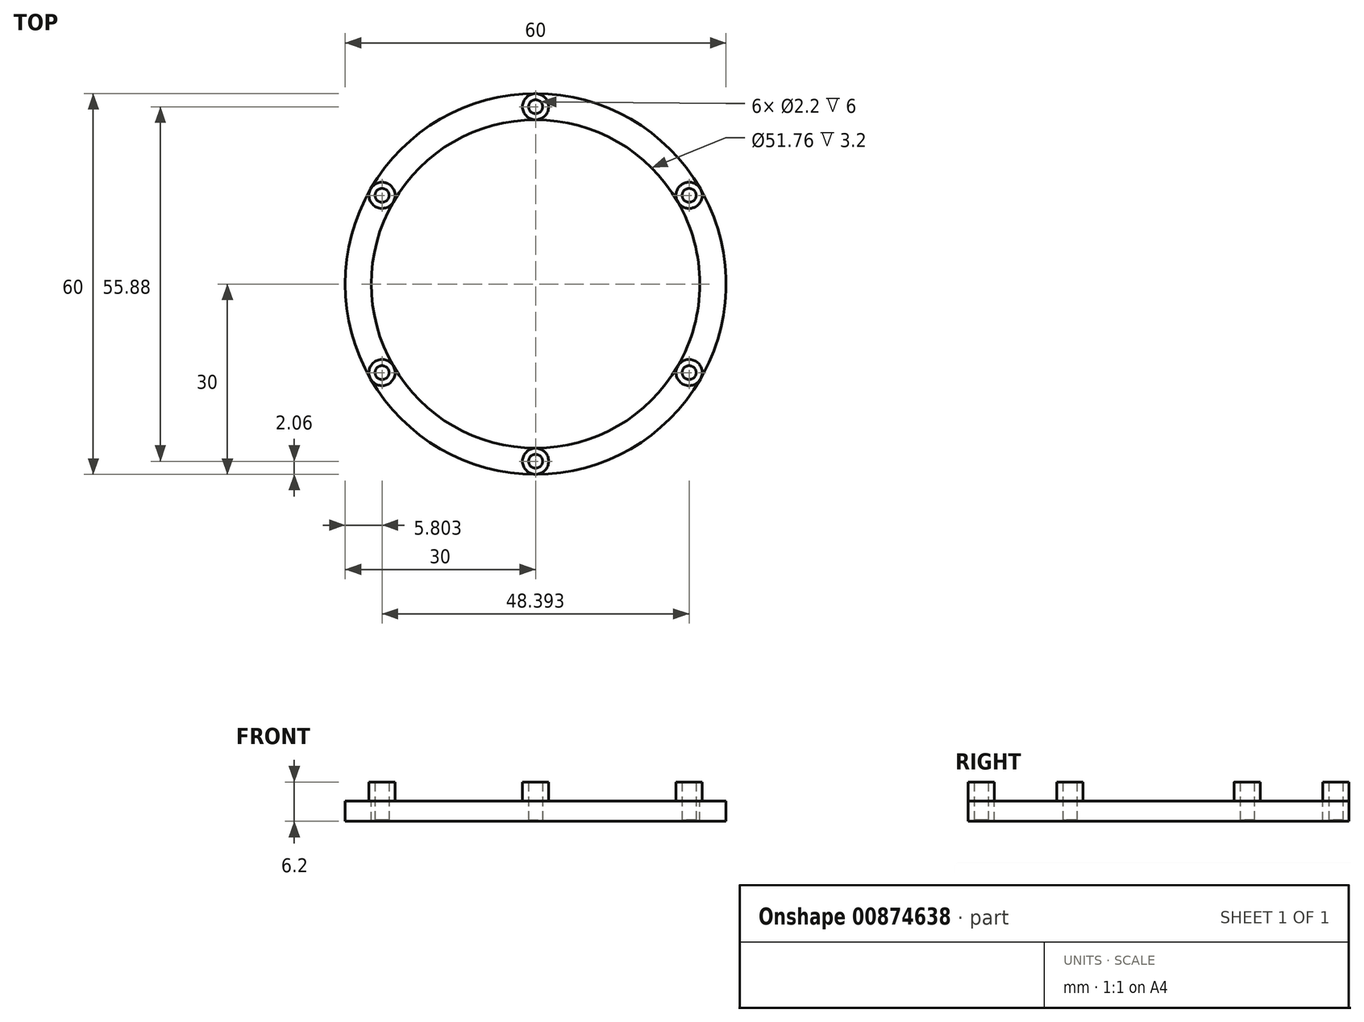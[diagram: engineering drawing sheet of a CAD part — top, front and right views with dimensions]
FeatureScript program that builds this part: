
annotation { "Feature Type Name" : "Feature", "Feature Type Description" : "" }
export const myFeature = defineFeature(function(context is Context, id is Id, definition is map)
    precondition{}
    {
        {
            assignVariable(context, id + "F0", {"name" : "numHoles", "anyValue" : 6});
        }
        {
            var Q0;
            Q0=qCreatedBy(makeId("Top.planeOp"),FACE);
            var sketch = newSketch(context, id + "F1", { "sketchPlane" : qUnion([Q0])});
            skCircle(sketch, "E0", {"center": v(0, 0) * mm, "radius": 30 * mm});
            skCircle(sketch, "E1", {"center": v(0, 0) * mm, "radius": 25.88 * mm});
            skLineSegment(sketch, "E2", {"start": v(0, 21.68) * mm, "end": v(0, -38.1) * mm, "construction": true});
            skCircle(sketch, "E3", {"center": v(0, 27.94) * mm, "radius": 1.1 * mm});
            skCircle(sketch, "E4", {"center": v(0, 27.94) * mm, "radius": 2.06 * mm});
            skLineSegment(sketch, "E5", {"start": v(0, 30) * mm, "end": v(0, 25.88) * mm, "construction": true});
            skSolve(sketch);
        }
        {
            var Q0;
            Q0=qCreatedBy(makeId("Right.planeOp"),FACE);
            var sketch = newSketch(context, id + "F2", { "sketchPlane" : qUnion([Q0])});
            skLineSegment(sketch, "E6", {"start": v(0, 37.6) * mm, "end": v(0, -34.54) * mm, "construction": true});
            skSolve(sketch);
        }
        {
            var Q0;
            {var subQ0=sQuery(id+"F1.wireOp",EDGE,"E0");Q0=makeQuery(id+"F1.imprint","IMPRINT",FACE,{"disambiguationData":[TD([[makeQuery(id+"F1.imprint","IMPRINT",EDGE,{"derivedFrom":subQ0}),1.0]])]});}
            var Q1;
            Q1=makeQuery(id+"F1.imprint","IMPRINT",FACE,{"disambiguationData":[TD([[makeQuery(id+"F1.imprint","IMPRINT",EDGE,{"derivedFrom":sQuery(id+"F1.wireOp",EDGE,"E3")}),-1.0]])]});
            var Q2;
            Q2=makeQuery(id+"F1.imprint","IMPRINT",FACE,{"disambiguationData":[TD([[makeQuery(id+"F1.imprint","IMPRINT",EDGE,{"derivedFrom":sQuery(id+"F1.wireOp",EDGE,"E3")}),1.0]])]});
            extrude(context, id + "F3", {"entities" : qUnion([Q0, Q1, Q2]), "oppositeDirection" : true, "depth" : 0.2 * mm, "offsetDistance" : 25 * mm});
        }
        {
            var Q0;
            {var subQ0=sQuery(id+"F1.wireOp",EDGE,"E0");Q0=makeQuery(id+"F1.imprint","IMPRINT",FACE,{"disambiguationData":[TD([[makeQuery(id+"F1.imprint","IMPRINT",EDGE,{"derivedFrom":subQ0}),1.0]])]});}
            var Q1;
            Q1=makeQuery(id+"F1.imprint","IMPRINT",FACE,{"disambiguationData":[TD([[makeQuery(id+"F1.imprint","IMPRINT",EDGE,{"derivedFrom":sQuery(id+"F1.wireOp",EDGE,"E3")}),-1.0]])]});
            var Q2;
            Q2=makeQuery(id+"F1.imprint","IMPRINT",FACE,{"disambiguationData":[TD([[makeQuery(id+"F1.imprint","IMPRINT",EDGE,{"derivedFrom":sQuery(id+"F1.wireOp",EDGE,"E3")}),1.0]])]});
            extrude(context, id + "F4", {"entities" : qUnion([Q0, Q1, Q2]), "depth" : 3 * mm, "offsetDistance" : 25 * mm});
        }
        {
            var Q0;
            Q0=makeQuery(id+"F1.imprint","IMPRINT",FACE,{"disambiguationData":[TD([[makeQuery(id+"F1.imprint","IMPRINT",EDGE,{"derivedFrom":sQuery(id+"F1.wireOp",EDGE,"E3")}),1.0]])]});
            extrude(context, id + "F5", {"entities" : qUnion([Q0]), "depth" : 25 * mm, "offsetDistance" : 25 * mm});
        }
        {
            var Q0;
            Q0=makeQuery(id+"F5.opExtrude","SWEPT_BODY",BODY,{"disambiguationData":[OSD([sQuery(id+"F1.wireOp",EDGE,"E3")])]});
            var Q1;
            Q1=sQuery(id+"F2.wireOp",EDGE,"E6");
            circularPattern(context, id + "F6", {"operationType" : NewBodyOperationType.REMOVE, "entities" : qUnion([Q0]), "axis" : qUnion([Q1]), "angle" : 360 * degree, "instanceCount" : getVariable(context, 'numHoles'), "equalSpace" : true});
        }
        {
            var Q0;
            Q0=makeQuery(id+"F1.imprint","IMPRINT",FACE,{"disambiguationData":[TD([[makeQuery(id+"F1.imprint","IMPRINT",EDGE,{"derivedFrom":sQuery(id+"F1.wireOp",EDGE,"E3")}),-1.0]])]});
            extrude(context, id + "F7", {"entities" : qUnion([Q0]), "depth" : 6 * mm, "offsetDistance" : 25 * mm});
        }
        {
            var Q0;
            Q0=makeQuery(id+"F7.opExtrude","SWEPT_BODY",BODY,{"disambiguationData":[OSD([sQuery(id+"F1.wireOp",EDGE,"E3"),sQuery(id+"F1.wireOp",EDGE,"E4")])]});
            var Q1;
            Q1=sQuery(id+"F2.wireOp",EDGE,"E6");
            circularPattern(context, id + "F8", {"operationType" : NewBodyOperationType.ADD, "entities" : qUnion([Q0]), "axis" : qUnion([Q1]), "angle" : 360 * degree, "instanceCount" : getVariable(context, 'numHoles'), "equalSpace" : true});
        }
    });
